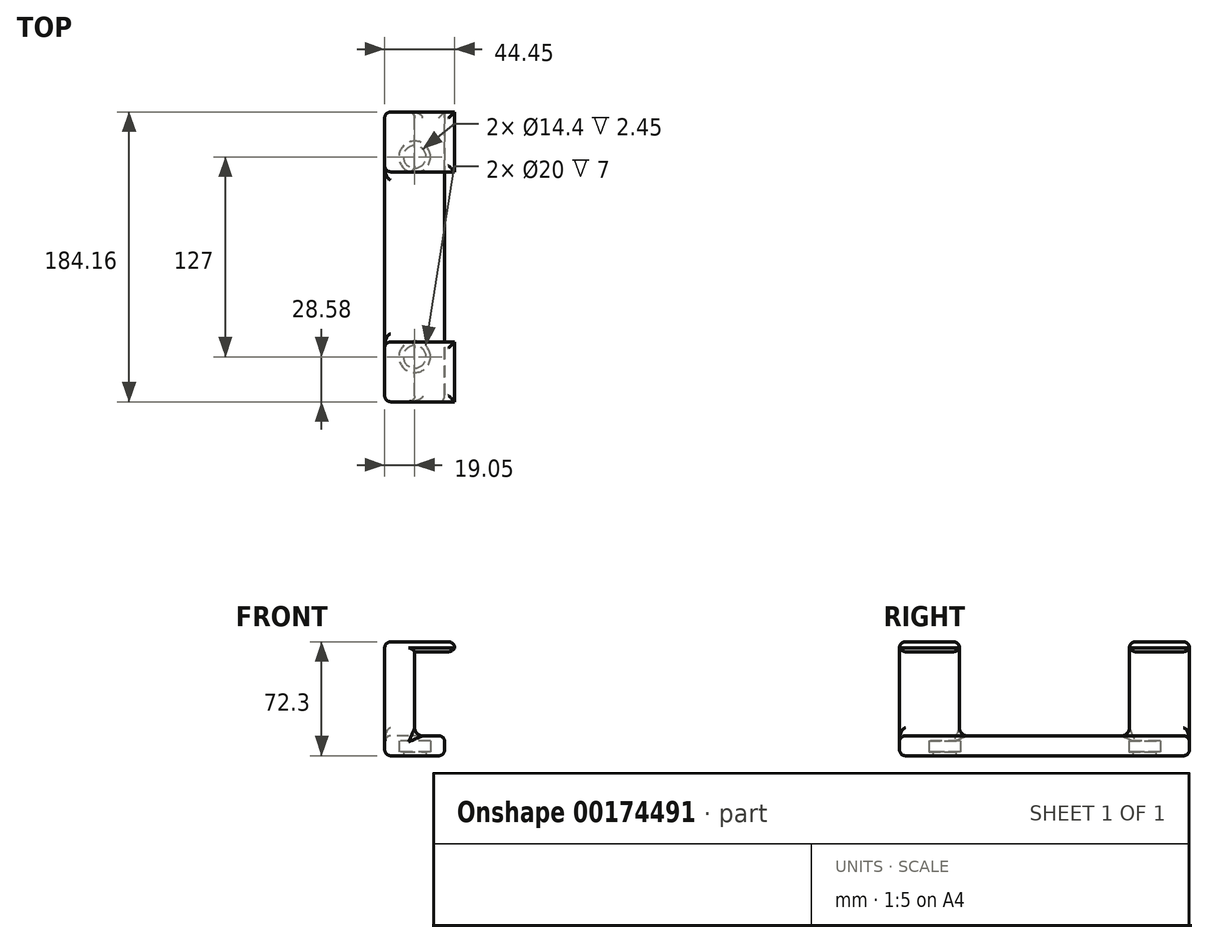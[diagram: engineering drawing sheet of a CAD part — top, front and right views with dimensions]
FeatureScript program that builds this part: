
annotation { "Feature Type Name" : "Feature", "Feature Type Description" : "" }
export const myFeature = defineFeature(function(context is Context, id is Id, definition is map)
    precondition{}
    {
        {
            var Q0;
            Q0=qCreatedBy(makeId("Top.planeOp"),FACE);
            var sketch = newSketch(context, id + "F0", { "sketchPlane" : qUnion([Q0])});
            skLineSegment(sketch, "E0.bottom", {"start": v(-19.05, -92.07) * mm, "end": v(19.05, -92.07) * mm});
            skLineSegment(sketch, "E0.top", {"start": v(-19.05, 92.08) * mm, "end": v(19.05, 92.08) * mm});
            skLineSegment(sketch, "E0.left", {"start": v(-19.05, -92.07) * mm, "end": v(-19.05, 92.08) * mm});
            skLineSegment(sketch, "E0.right", {"start": v(19.05, -92.07) * mm, "end": v(19.05, 92.08) * mm});
            skPoint(sketch, "E0.middle", {"position": v(0, 0) * mm});
            skSolve(sketch);
        }
        {
            var Q0;
            Q0 = qSketchRegion(id + "F0", true);
            extrude(context, id + "F1", {"entities" : qUnion([Q0]), "depth" : 10.16 * mm});
        }
        {
            var Q0;
            Q0=qCreatedBy(makeId("Top.planeOp"),FACE);
            cPlane(context, id + "F2", {"entities" : qUnion([Q0]), "cplaneType" : CPlaneType.OFFSET, "offset" : 6.35 * mm, "width" : 152.4 * mm, "height" : 152.4 * mm});
        }
        {
            var Q0;
            Q0=qCreatedBy(id+"F2.planeOp",FACE);
            var sketch = newSketch(context, id + "F3", { "sketchPlane" : qUnion([Q0])});
            skLineSegment(sketch, "E1.bottom", {"start": v(-19.05, 92.08) * mm, "end": v(0, 92.08) * mm});
            skLineSegment(sketch, "E1.top", {"start": v(-19.05, 53.98) * mm, "end": v(0, 53.98) * mm});
            skLineSegment(sketch, "E1.left", {"start": v(-19.05, 92.08) * mm, "end": v(-19.05, 53.98) * mm});
            skLineSegment(sketch, "E1.right", {"start": v(0, 92.08) * mm, "end": v(0, 53.98) * mm});
            skLineSegment(sketch, "E2.bottom", {"start": v(-19.05, -53.98) * mm, "end": v(0, -53.97) * mm});
            skLineSegment(sketch, "E2.top", {"start": v(-19.05, -92.07) * mm, "end": v(0, -92.07) * mm});
            skLineSegment(sketch, "E2.left", {"start": v(-19.05, -53.97) * mm, "end": v(-19.05, -92.07) * mm});
            skLineSegment(sketch, "E2.right", {"start": v(0, -53.98) * mm, "end": v(0, -92.07) * mm});
            skSolve(sketch);
        }
        {
            var Q0;
            Q0 = qSketchRegion(id + "F3", true);
            extrude(context, id + "F4", {"entities" : qUnion([Q0]), "operationType" : NewBodyOperationType.ADD, "depth" : 63.5 * mm});
        }
        {
            var Q0;
            Q0=qCreatedBy(makeId("Right.planeOp"),FACE);
            var sketch = newSketch(context, id + "F5", { "sketchPlane" : qUnion([Q0])});
            skLineSegment(sketch, "E3.bottom", {"start": v(-92.07, 69.85) * mm, "end": v(-53.97, 69.85) * mm});
            skLineSegment(sketch, "E3.top", {"start": v(-92.07, 63.5) * mm, "end": v(-53.97, 63.5) * mm});
            skLineSegment(sketch, "E3.left", {"start": v(-53.97, 69.85) * mm, "end": v(-53.97, 63.5) * mm});
            skLineSegment(sketch, "E3.right", {"start": v(-92.07, 69.85) * mm, "end": v(-92.07, 63.5) * mm});
            skLineSegment(sketch, "E4.bottom", {"start": v(53.98, 69.85) * mm, "end": v(92.08, 69.85) * mm});
            skLineSegment(sketch, "E4.top", {"start": v(53.98, 63.5) * mm, "end": v(92.08, 63.5) * mm});
            skLineSegment(sketch, "E4.left", {"start": v(53.98, 69.85) * mm, "end": v(53.98, 63.5) * mm});
            skLineSegment(sketch, "E4.right", {"start": v(92.08, 69.85) * mm, "end": v(92.08, 63.5) * mm});
            skSolve(sketch);
        }
        {
            var Q0;
            Q0 = qSketchRegion(id + "F5", true);
            extrude(context, id + "F6", {"entities" : qUnion([Q0]), "operationType" : NewBodyOperationType.ADD, "depth" : 25.4 * mm});
        }
        {
            var Q0;
            Q0=qCreatedBy(makeId("Top.planeOp"),FACE);
            var sketch = newSketch(context, id + "F7", { "sketchPlane" : qUnion([Q0])});
            skCircle(sketch, "E5", {"center": v(0, -63.5) * mm, "radius": 10 * mm});
            skCircle(sketch, "E6", {"center": v(0, 63.5) * mm, "radius": 10 * mm});
            skSolve(sketch);
        }
        {
            var Q0;
            Q0=makeQuery(id+"F7.imprint","IMPRINT",FACE,{"disambiguationData":[TD([[makeQuery(id+"F7.imprint","IMPRINT",EDGE,{"derivedFrom":sQuery(id+"F7.wireOp",EDGE,"E6")}),1.0]])]});
            var Q1;
            Q1=makeQuery(id+"F7.imprint","IMPRINT",FACE,{"disambiguationData":[TD([[makeQuery(id+"F7.imprint","IMPRINT",EDGE,{"derivedFrom":sQuery(id+"F7.wireOp",EDGE,"E5")}),1.0]])]});
            extrude(context, id + "F8", {"entities" : qUnion([Q0, Q1]), "operationType" : NewBodyOperationType.REMOVE, "depth" : 7 * mm});
        }
        {
            var Q0;
            Q0=qCreatedBy(makeId("Top.planeOp"),FACE);
            var sketch = newSketch(context, id + "F9", { "sketchPlane" : qUnion([Q0])});
            skLineSegment(sketch, "E7.bottom", {"start": v(-19.05, 92.08) * mm, "end": v(19.05, 92.08) * mm});
            skLineSegment(sketch, "E7.top", {"start": v(-19.05, -92.08) * mm, "end": v(19.05, -92.08) * mm});
            skLineSegment(sketch, "E7.left", {"start": v(-19.05, 92.08) * mm, "end": v(-19.05, -92.08) * mm});
            skLineSegment(sketch, "E7.right", {"start": v(19.05, 92.08) * mm, "end": v(19.05, -92.08) * mm});
            skPoint(sketch, "E7.middle", {"position": v(0, 0) * mm});
            skSolve(sketch);
        }
        {
            var Q0;
            Q0 = qSketchRegion(id + "F9", true);
            extrude(context, id + "F10", {"entities" : qUnion([Q0]), "operationType" : NewBodyOperationType.ADD, "oppositeDirection" : true, "depth" : 2.45 * mm});
        }
        {
            var Q0;
            Q0=makeQuery(id+"F10.opExtrude","CAP_FACE",FACE,{"disambiguationData":[OSD([sQuery(id+"F9.wireOp",EDGE,"E7.bottom"),sQuery(id+"F9.wireOp",EDGE,"E7.top"),sQuery(id+"F9.wireOp",EDGE,"E7.left"),sQuery(id+"F9.wireOp",EDGE,"E7.right")])],"isStart":false});
            var sketch = newSketch(context, id + "F11", { "sketchPlane" : qUnion([Q0])});
            skCircle(sketch, "E8", {"center": v(0, -63.5) * mm, "radius": 7.2 * mm});
            skCircle(sketch, "E9", {"center": v(0, 63.5) * mm, "radius": 7.2 * mm});
            skSolve(sketch);
        }
        {
            var Q0;
            Q0 = qSketchRegion(id + "F11", true);
            extrude(context, id + "F12", {"entities" : qUnion([Q0]), "operationType" : NewBodyOperationType.REMOVE, "oppositeDirection" : true, "depth" : 2.55 * mm});
        }
        {
            var Q0;
            Q0=makeQuery(id+"F10.opExtrude","CAP_EDGE",EDGE,{"disambiguationData":[OSD([sQuery(id+"F9.wireOp",EDGE,"E7.bottom")])],"isStart":false});
            var Q1;
            Q1=makeQuery(id+"F1.opExtrude","CAP_EDGE",EDGE,{"disambiguationData":[OSD([sQuery(id+"F0.wireOp",EDGE,"E0.top")])],"isStart":false});
            var Q2;
            Q2=makeQuery(id+"F4.opExtrude","SWEPT_EDGE",EDGE,{"disambiguationData":[OSD([sQuery(id+"F3.wireOp",EDGE,"E1.bottom"),sQuery(id+"F3.wireOp",EDGE,"E1.right")])]});
            var Q3;
            Q3=makeQuery(id+"F10.boolean.opBoolean","MERGE",EDGE,{"derivedFrom":[makeQuery(id+"F4.boolean.opBoolean","MERGE",EDGE,{"derivedFrom":[makeQuery(id+"F1.opExtrude","SWEPT_EDGE",EDGE,{"disambiguationData":[OSD([sQuery(id+"F0.wireOp",EDGE,"E0.top"),sQuery(id+"F0.wireOp",EDGE,"E0.left")])]}),makeQuery(id+"F4.opExtrude","SWEPT_EDGE",EDGE,{"disambiguationData":[OSD([sQuery(id+"F3.wireOp",EDGE,"E1.bottom"),sQuery(id+"F3.wireOp",EDGE,"E1.left")])]})]}),makeQuery(id+"F10.opExtrude","SWEPT_EDGE",EDGE,{"disambiguationData":[OSD([sQuery(id+"F9.wireOp",EDGE,"E7.bottom"),sQuery(id+"F9.wireOp",EDGE,"E7.left")])]})]});
            var Q4;
            Q4=makeQuery(id+"F6.boolean.opBoolean","MERGE",EDGE,{"derivedFrom":[makeQuery(id+"F4.opExtrude","CAP_EDGE",EDGE,{"disambiguationData":[OSD([sQuery(id+"F3.wireOp",EDGE,"E1.bottom")])],"isStart":false}),makeQuery(id+"F6.opExtrude","SWEPT_EDGE",EDGE,{"disambiguationData":[OSD([sQuery(id+"F5.wireOp",EDGE,"E4.bottom"),sQuery(id+"F5.wireOp",EDGE,"E4.right")])]})]});
            var Q5;
            Q5=makeQuery(id+"F4.opExtrude","CAP_EDGE",EDGE,{"disambiguationData":[OSD([sQuery(id+"F3.wireOp",EDGE,"E1.left")])],"isStart":false});
            var Q6;
            Q6=makeQuery(id+"F6.opExtrude","CAP_EDGE",EDGE,{"disambiguationData":[OSD([sQuery(id+"F5.wireOp",EDGE,"E4.bottom")])],"isStart":false});
            var Q7;
            Q7=makeQuery(id+"F6.boolean.opBoolean","MERGE",EDGE,{"derivedFrom":[makeQuery(id+"F4.opExtrude","CAP_EDGE",EDGE,{"disambiguationData":[OSD([sQuery(id+"F3.wireOp",EDGE,"E1.top")])],"isStart":false}),makeQuery(id+"F6.opExtrude","SWEPT_EDGE",EDGE,{"disambiguationData":[OSD([sQuery(id+"F5.wireOp",EDGE,"E4.bottom"),sQuery(id+"F5.wireOp",EDGE,"E4.left")])]})]});
            var Q8;
            Q8=makeQuery(id+"F6.boolean.opBoolean","MERGE",EDGE,{"derivedFrom":[makeQuery(id+"F4.opExtrude","CAP_EDGE",EDGE,{"disambiguationData":[OSD([sQuery(id+"F3.wireOp",EDGE,"E2.top")])],"isStart":false}),makeQuery(id+"F6.opExtrude","SWEPT_EDGE",EDGE,{"disambiguationData":[OSD([sQuery(id+"F5.wireOp",EDGE,"E3.bottom"),sQuery(id+"F5.wireOp",EDGE,"E3.right")])]})]});
            var Q9;
            Q9=makeQuery(id+"F6.opExtrude","CAP_EDGE",EDGE,{"disambiguationData":[OSD([sQuery(id+"F5.wireOp",EDGE,"E3.bottom")])],"isStart":false});
            var Q10;
            Q10=makeQuery(id+"F6.boolean.opBoolean","MERGE",EDGE,{"derivedFrom":[makeQuery(id+"F4.opExtrude","CAP_EDGE",EDGE,{"disambiguationData":[OSD([sQuery(id+"F3.wireOp",EDGE,"E2.bottom")])],"isStart":false}),makeQuery(id+"F6.opExtrude","SWEPT_EDGE",EDGE,{"disambiguationData":[OSD([sQuery(id+"F5.wireOp",EDGE,"E3.bottom"),sQuery(id+"F5.wireOp",EDGE,"E3.left")])]})]});
            var Q11;
            Q11=makeQuery(id+"F4.opExtrude","CAP_EDGE",EDGE,{"disambiguationData":[OSD([sQuery(id+"F3.wireOp",EDGE,"E2.left")])],"isStart":false});
            var Q12;
            Q12=makeQuery(id+"F1.opExtrude","CAP_EDGE",EDGE,{"disambiguationData":[OSD([sQuery(id+"F0.wireOp",EDGE,"E0.bottom")])],"isStart":false});
            var Q13;
            Q13=makeQuery(id+"F4.opExtrude","SWEPT_EDGE",EDGE,{"disambiguationData":[OSD([sQuery(id+"F3.wireOp",EDGE,"E2.top"),sQuery(id+"F3.wireOp",EDGE,"E2.right")])]});
            var Q14;
            Q14=makeQuery(id+"F4.opExtrude","SWEPT_EDGE",EDGE,{"disambiguationData":[OSD([sQuery(id+"F3.wireOp",EDGE,"E2.top"),sQuery(id+"F3.wireOp",EDGE,"E2.left")])]});
            var Q15;
            Q15=makeQuery(id+"F10.boolean.opBoolean","MERGE",EDGE,{"derivedFrom":[makeQuery(id+"F1.opExtrude","SWEPT_EDGE",EDGE,{"disambiguationData":[OSD([sQuery(id+"F0.wireOp",EDGE,"E0.bottom"),sQuery(id+"F0.wireOp",EDGE,"E0.left")])]}),makeQuery(id+"F10.opExtrude","SWEPT_EDGE",EDGE,{"disambiguationData":[OSD([sQuery(id+"F9.wireOp",EDGE,"E7.top"),sQuery(id+"F9.wireOp",EDGE,"E7.left")])]})]});
            var Q16;
            Q16=makeQuery(id+"F10.boolean.opBoolean","MERGE",EDGE,{"derivedFrom":[makeQuery(id+"F1.opExtrude","SWEPT_EDGE",EDGE,{"disambiguationData":[OSD([sQuery(id+"F0.wireOp",EDGE,"E0.bottom"),sQuery(id+"F0.wireOp",EDGE,"E0.right")])]}),makeQuery(id+"F10.opExtrude","SWEPT_EDGE",EDGE,{"disambiguationData":[OSD([sQuery(id+"F9.wireOp",EDGE,"E7.top"),sQuery(id+"F9.wireOp",EDGE,"E7.right")])]})]});
            var Q17;
            Q17=makeQuery(id+"F10.opExtrude","CAP_EDGE",EDGE,{"disambiguationData":[OSD([sQuery(id+"F9.wireOp",EDGE,"E7.top")])],"isStart":false});
            var Q18;
            Q18=makeQuery(id+"F1.opExtrude","CAP_EDGE",EDGE,{"disambiguationData":[OSD([sQuery(id+"F0.wireOp",EDGE,"E0.right")])],"isStart":false});
            var Q19;
            Q19=makeQuery(id+"F10.opExtrude","CAP_EDGE",EDGE,{"disambiguationData":[OSD([sQuery(id+"F9.wireOp",EDGE,"E7.right")])],"isStart":false});
            var Q20;
            Q20=makeQuery(id+"F10.opExtrude","CAP_EDGE",EDGE,{"disambiguationData":[OSD([sQuery(id+"F9.wireOp",EDGE,"E7.left")])],"isStart":false});
            var Q21;
            Q21=makeQuery(id+"F4.opExtrude","SWEPT_EDGE",EDGE,{"disambiguationData":[OSD([sQuery(id+"F3.wireOp",EDGE,"E1.top"),sQuery(id+"F3.wireOp",EDGE,"E1.left")])]});
            var Q22;
            Q22=makeQuery(id+"F4.opExtrude","SWEPT_EDGE",EDGE,{"disambiguationData":[OSD([sQuery(id+"F3.wireOp",EDGE,"E1.top"),sQuery(id+"F3.wireOp",EDGE,"E1.right")])]});
            var Q23;
            {var subQ0=sQuery(id+"F0.wireOp",EDGE,"E0.left");Q23=makeQuery(id+"F4.boolean.opBoolean","SPLIT",EDGE,{"disambiguationData":[TD([makeQuery(id+"F4.opExtrude","SWEPT_FACE",FACE,{"disambiguationData":[OSD([sQuery(id+"F3.wireOp",EDGE,"E1.top")])]})])],"derivedFrom":makeQuery(id+"F1.opExtrude","CAP_EDGE",EDGE,{"disambiguationData":[OSD([subQ0])],"isStart":false})});}
            var Q24;
            Q24=makeQuery(id+"F4.opExtrude","SWEPT_EDGE",EDGE,{"disambiguationData":[OSD([sQuery(id+"F3.wireOp",EDGE,"E2.bottom"),sQuery(id+"F3.wireOp",EDGE,"E2.left")])]});
            var Q25;
            Q25=makeQuery(id+"F4.opExtrude","SWEPT_EDGE",EDGE,{"disambiguationData":[OSD([sQuery(id+"F3.wireOp",EDGE,"E2.bottom"),sQuery(id+"F3.wireOp",EDGE,"E2.right")])]});
            fillet(context, id + "F13", {"entities" : qUnion([Q0, Q1, Q2, Q3, Q4, Q5, Q6, Q7, Q8, Q9, Q10, Q11, Q12, Q13, Q14, Q15, Q16, Q17, Q18, Q19, Q20, Q21, Q22, Q23, Q24, Q25]), "radius" : 3.8 * mm, "tangentPropagation" : true, "allowEdgeOverflow" : false});
        }
        {
            var Q0;
            Q0=makeQuery(id+"F6.opExtrude","CAP_EDGE",EDGE,{"disambiguationData":[OSD([sQuery(id+"F5.wireOp",EDGE,"E4.top")])],"isStart":false});
            var Q1;
            Q1=makeQuery(id+"F6.opExtrude","CAP_EDGE",EDGE,{"disambiguationData":[OSD([sQuery(id+"F5.wireOp",EDGE,"E3.top")])],"isStart":false});
            var Q2;
            Q2=makeQuery(id+"F6.opExtrude","SWEPT_EDGE",EDGE,{"disambiguationData":[OSD([sQuery(id+"F5.wireOp",EDGE,"E3.top"),sQuery(id+"F5.wireOp",EDGE,"E3.right")])]});
            var Q3;
            Q3=makeQuery(id+"F6.opExtrude","SWEPT_EDGE",EDGE,{"disambiguationData":[OSD([sQuery(id+"F5.wireOp",EDGE,"E3.top"),sQuery(id+"F5.wireOp",EDGE,"E3.left")])]});
            var Q4;
            Q4=makeQuery(id+"F6.opExtrude","SWEPT_EDGE",EDGE,{"disambiguationData":[OSD([sQuery(id+"F5.wireOp",EDGE,"E4.top"),sQuery(id+"F5.wireOp",EDGE,"E4.left")])]});
            var Q5;
            Q5=makeQuery(id+"F6.opExtrude","SWEPT_EDGE",EDGE,{"disambiguationData":[OSD([sQuery(id+"F5.wireOp",EDGE,"E4.top"),sQuery(id+"F5.wireOp",EDGE,"E4.right")])]});
            fillet(context, id + "F14", {"entities" : qUnion([Q0, Q1, Q2, Q3, Q4, Q5]), "radius" : 5.08 * mm, "tangentPropagation" : true, "allowEdgeOverflow" : false});
        }
        {
            var Q0;
            Q0=makeQuery(id+"F4.boolean.opBoolean","INTERSECT",EDGE,{"derivedFrom":[makeQuery(id+"F1.opExtrude","CAP_FACE",FACE,{"disambiguationData":[OSD([sQuery(id+"F0.wireOp",EDGE,"E0.bottom"),sQuery(id+"F0.wireOp",EDGE,"E0.top"),sQuery(id+"F0.wireOp",EDGE,"E0.left"),sQuery(id+"F0.wireOp",EDGE,"E0.right")])],"isStart":false}),makeQuery(id+"F4.opExtrude","SWEPT_FACE",FACE,{"disambiguationData":[OSD([sQuery(id+"F3.wireOp",EDGE,"E1.right")])]})]});
            var Q1;
            Q1=makeQuery(id+"F4.boolean.opBoolean","INTERSECT",EDGE,{"derivedFrom":[makeQuery(id+"F1.opExtrude","CAP_FACE",FACE,{"disambiguationData":[OSD([sQuery(id+"F0.wireOp",EDGE,"E0.bottom"),sQuery(id+"F0.wireOp",EDGE,"E0.top"),sQuery(id+"F0.wireOp",EDGE,"E0.left"),sQuery(id+"F0.wireOp",EDGE,"E0.right")])],"isStart":false}),makeQuery(id+"F4.opExtrude","SWEPT_FACE",FACE,{"disambiguationData":[OSD([sQuery(id+"F3.wireOp",EDGE,"E2.right")])]})]});
            var Q2;
            Q2=makeQuery(id+"F4.boolean.opBoolean","INTERSECT",EDGE,{"derivedFrom":[makeQuery(id+"F1.opExtrude","CAP_FACE",FACE,{"disambiguationData":[OSD([sQuery(id+"F0.wireOp",EDGE,"E0.bottom"),sQuery(id+"F0.wireOp",EDGE,"E0.top"),sQuery(id+"F0.wireOp",EDGE,"E0.left"),sQuery(id+"F0.wireOp",EDGE,"E0.right")])],"isStart":false}),makeQuery(id+"F4.opExtrude","SWEPT_FACE",FACE,{"disambiguationData":[OSD([sQuery(id+"F3.wireOp",EDGE,"E2.bottom")])]})]});
            var Q3;
            Q3=makeQuery(id+"F4.boolean.opBoolean","INTERSECT",EDGE,{"derivedFrom":[makeQuery(id+"F1.opExtrude","CAP_FACE",FACE,{"disambiguationData":[OSD([sQuery(id+"F0.wireOp",EDGE,"E0.bottom"),sQuery(id+"F0.wireOp",EDGE,"E0.top"),sQuery(id+"F0.wireOp",EDGE,"E0.left"),sQuery(id+"F0.wireOp",EDGE,"E0.right")])],"isStart":false}),makeQuery(id+"F4.opExtrude","SWEPT_FACE",FACE,{"disambiguationData":[OSD([sQuery(id+"F3.wireOp",EDGE,"E1.top")])]})]});
            fillet(context, id + "F15", {"entities" : qUnion([Q0, Q1, Q2, Q3]), "radius" : 5.08 * mm, "tangentPropagation" : true, "allowEdgeOverflow" : false});
        }
    });
